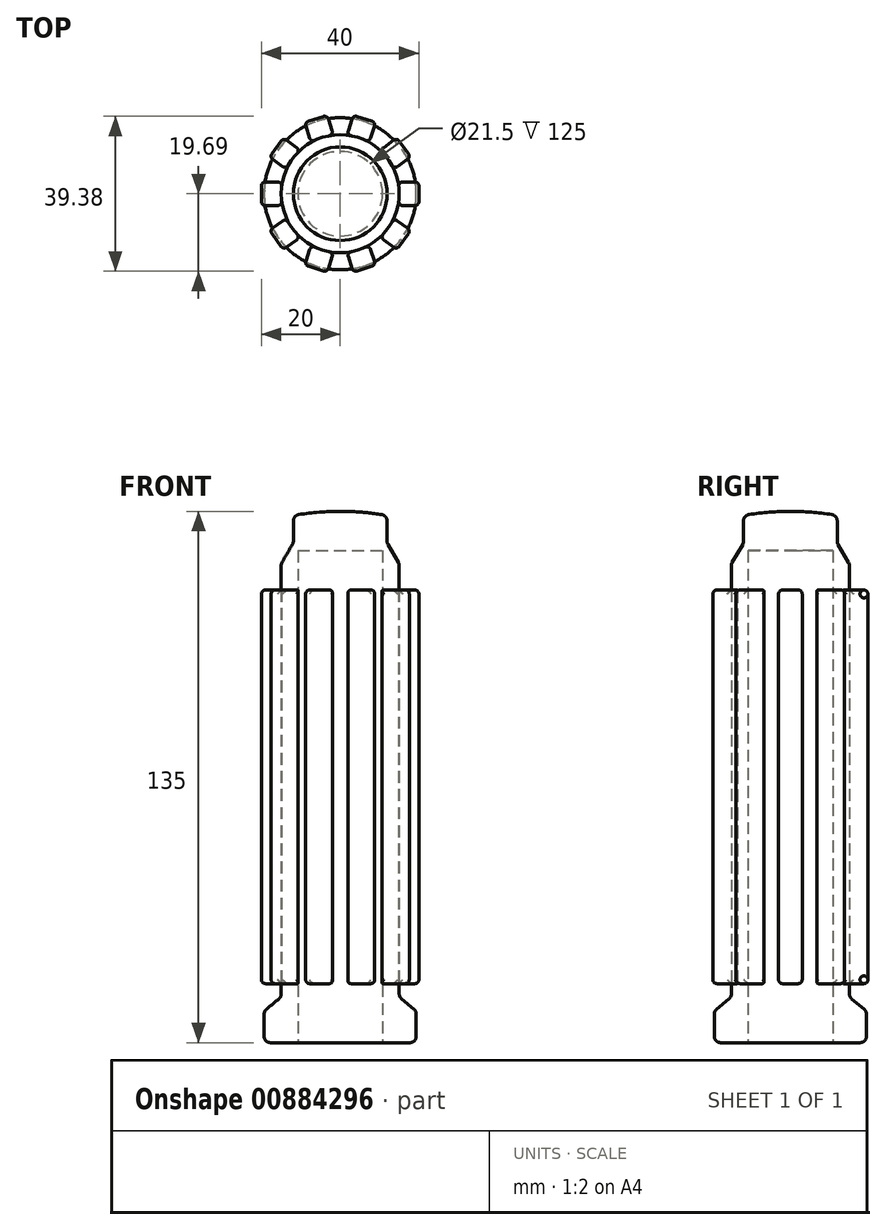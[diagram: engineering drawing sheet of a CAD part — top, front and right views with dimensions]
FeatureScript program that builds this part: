
annotation { "Feature Type Name" : "Feature", "Feature Type Description" : "" }
export const myFeature = defineFeature(function(context is Context, id is Id, definition is map)
    precondition{}
    {
        {
            var Q0;
            Q0=qCreatedBy(makeId("Front.planeOp"),FACE);
            var sketch = newSketch(context, id + "F0", { "sketchPlane" : qUnion([Q0])});
            skLineSegment(sketch, "E0", {"start": v(10.75, 0) * mm, "end": v(19.33, 0) * mm});
            skLineSegment(sketch, "E1", {"start": v(19.32, 0) * mm, "end": v(19.32, 8) * mm});
            skLineSegment(sketch, "E2", {"start": v(19.32, 8) * mm, "end": v(15, 11.63) * mm});
            skLineSegment(sketch, "E3", {"start": v(15, 11.63) * mm, "end": v(15, 121.63) * mm});
            skLineSegment(sketch, "E4", {"start": v(15, 121.63) * mm, "end": v(11.9, 127) * mm});
            skLineSegment(sketch, "E5", {"start": v(11.9, 127) * mm, "end": v(11.9, 133.95) * mm});
            skLineSegment(sketch, "E6", {"start": v(10.75, 0) * mm, "end": v(10.75, 125) * mm});
            skLineSegment(sketch, "E7", {"start": v(10.75, 125) * mm, "end": v(0, 125) * mm});
            skLineSegment(sketch, "E8", {"start": v(0, 125) * mm, "end": v(0, 135) * mm});
            skArc(sketch, "E9", {"start": v(11.9, 133.95) * mm, "mid": v(5.97, 134.74) * mm, "end": v(0, 135) * mm});
            skLineSegment(sketch, "E10", {"start": v(0, 0) * mm, "end": v(0, 133.97) * mm, "construction": true});
            skSolve(sketch);
        }
        {
            var Q0;
            Q0=qSketchRegion(id+"F0",true);
            var Q1;
            Q1=sQuery(id+"F0.wireOp",EDGE,"E10");
            revolve(context, id + "F1", {"surfaceOperationType" : NewSurfaceOperationType.NEW, "entities" : qUnion([Q0]), "axis" : qUnion([Q1]), "revolveType" : RevolveType.FULL});
        }
        {
            var Q0;
            Q0=makeQuery(id+"F1.opRevolve","SWEPT_EDGE",EDGE,{"disambiguationData":[OSD([sQuery(id+"F0.wireOp",EDGE,"E2"),sQuery(id+"F0.wireOp",EDGE,"E3")])]});
            var Q1;
            Q1=makeQuery(id+"F1.opRevolve","SWEPT_EDGE",EDGE,{"disambiguationData":[OSD([sQuery(id+"F0.wireOp",EDGE,"E1"),sQuery(id+"F0.wireOp",EDGE,"E2")])]});
            var Q2;
            Q2=makeQuery(id+"F1.opRevolve","SWEPT_EDGE",EDGE,{"disambiguationData":[OSD([sQuery(id+"F0.wireOp",EDGE,"E0"),sQuery(id+"F0.wireOp",EDGE,"E1")])]});
            var Q3;
            Q3=makeQuery(id+"F1.opRevolve","SWEPT_EDGE",EDGE,{"disambiguationData":[OSD([sQuery(id+"F0.wireOp",EDGE,"E3"),sQuery(id+"F0.wireOp",EDGE,"E4")])]});
            var Q4;
            Q4=makeQuery(id+"F1.opRevolve","SWEPT_EDGE",EDGE,{"disambiguationData":[OSD([sQuery(id+"F0.wireOp",EDGE,"E4"),sQuery(id+"F0.wireOp",EDGE,"E5")])]});
            var Q5;
            Q5=makeQuery(id+"F1.opRevolve","SWEPT_EDGE",EDGE,{"disambiguationData":[OSD([sQuery(id+"F0.wireOp",EDGE,"E5"),sQuery(id+"F0.wireOp",EDGE,"E9")])]});
            fillet(context, id + "F2", {"entities" : qUnion([Q0, Q1, Q2, Q3, Q4, Q5]), "radius" : 1.6 * mm, "tangentPropagation" : true, "allowEdgeOverflow" : false});
        }
        {
            var Q0;
            Q0=qCreatedBy(makeId("Right.planeOp"),FACE);
            cPlane(context, id + "F3", {"entities" : qUnion([Q0]), "cplaneType" : CPlaneType.OFFSET, "offset" : 20 * mm, "width" : 150 * mm, "height" : 150 * mm});
        }
        {
            var Q0;
            Q0=qCreatedBy(id+"F3.planeOp",FACE);
            var sketch = newSketch(context, id + "F4", { "sketchPlane" : qUnion([Q0])});
            skLineSegment(sketch, "E11.bottom", {"start": v(-3, 115) * mm, "end": v(3, 115) * mm});
            skLineSegment(sketch, "E11.top", {"start": v(-3, 15) * mm, "end": v(3, 15) * mm});
            skLineSegment(sketch, "E11.left", {"start": v(-3, 115) * mm, "end": v(-3, 15) * mm});
            skLineSegment(sketch, "E11.right", {"start": v(3, 115) * mm, "end": v(3, 15) * mm});
            skSolve(sketch);
        }
        {
            var Q0;
            Q0=qSketchRegion(id+"F4",true);
            var Q1;
            Q1=makeQuery(id+"F1.opRevolve","SWEPT_FACE",FACE,{"disambiguationData":[OSD([sQuery(id+"F0.wireOp",EDGE,"E3")])]});
            extrude(context, id + "F5", {"entities" : qUnion([Q0]), "endBound" : BoundingType.UP_TO_SURFACE, "oppositeDirection" : true, "depth" : 25 * mm, "endBoundEntityFace" : qUnion([Q1]), "offsetDistance" : 25 * mm});
        }
        {
            var Q0;
            Q0=makeQuery(id+"F5.opExtrude","CAP_EDGE",EDGE,{"disambiguationData":[OSD([sQuery(id+"F4.wireOp",EDGE,"E11.bottom")])],"isStart":true});
            var Q1;
            Q1=makeQuery(id+"F5.opExtrude","CAP_EDGE",EDGE,{"disambiguationData":[OSD([sQuery(id+"F4.wireOp",EDGE,"E11.left")])],"isStart":true});
            var Q2;
            Q2=makeQuery(id+"F5.opExtrude","CAP_EDGE",EDGE,{"disambiguationData":[OSD([sQuery(id+"F4.wireOp",EDGE,"E11.left")])],"isStart":false});
            var Q3;
            Q3=makeQuery(id+"F5.opExtrude","CAP_EDGE",EDGE,{"disambiguationData":[OSD([sQuery(id+"F4.wireOp",EDGE,"E11.right")])],"isStart":true});
            var Q4;
            Q4=makeQuery(id+"F5.opExtrude","CAP_EDGE",EDGE,{"disambiguationData":[OSD([sQuery(id+"F4.wireOp",EDGE,"E11.right")])],"isStart":false});
            var Q5;
            Q5=makeQuery(id+"F5.opExtrude","SWEPT_EDGE",EDGE,{"disambiguationData":[OSD([sQuery(id+"F4.wireOp",EDGE,"E11.top"),sQuery(id+"F4.wireOp",EDGE,"E11.right")])]});
            var Q6;
            Q6=makeQuery(id+"F5.opExtrude","CAP_EDGE",EDGE,{"disambiguationData":[OSD([sQuery(id+"F4.wireOp",EDGE,"E11.top")])],"isStart":true});
            var Q7;
            Q7=makeQuery(id+"F5.opExtrude","SWEPT_EDGE",EDGE,{"disambiguationData":[OSD([sQuery(id+"F4.wireOp",EDGE,"E11.bottom"),sQuery(id+"F4.wireOp",EDGE,"E11.right")])]});
            var Q8;
            Q8=makeQuery(id+"F5.opExtrude","SWEPT_EDGE",EDGE,{"disambiguationData":[OSD([sQuery(id+"F4.wireOp",EDGE,"E11.bottom"),sQuery(id+"F4.wireOp",EDGE,"E11.left")])]});
            var Q9;
            Q9=makeQuery(id+"F5.opExtrude","SWEPT_EDGE",EDGE,{"disambiguationData":[OSD([sQuery(id+"F4.wireOp",EDGE,"E11.top"),sQuery(id+"F4.wireOp",EDGE,"E11.left")])]});
            fillet(context, id + "F6", {"entities" : qUnion([Q0, Q1, Q2, Q3, Q4, Q5, Q6, Q7, Q8, Q9]), "radius" : 1 * mm, "tangentPropagation" : true, "allowEdgeOverflow" : false});
        }
        {
            var Q0;
            Q0=makeQuery(id+"F5.opExtrude","SWEPT_BODY",BODY,{"disambiguationData":[OSD([sQuery(id+"F4.wireOp",EDGE,"E11.bottom"),sQuery(id+"F4.wireOp",EDGE,"E11.top"),sQuery(id+"F4.wireOp",EDGE,"E11.left"),sQuery(id+"F4.wireOp",EDGE,"E11.right")])]});
            var Q1;
            Q1=sQuery(id+"F0.wireOp",EDGE,"E10");
            circularPattern(context, id + "F7", {"entities" : qUnion([Q0]), "axis" : qUnion([Q1]), "angle" : 360 * degree, "instanceCount" : 10, "equalSpace" : true});
        }
    });
